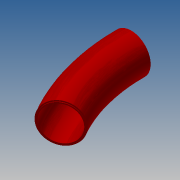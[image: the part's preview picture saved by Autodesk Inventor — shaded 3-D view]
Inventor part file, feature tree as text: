
AUTODESK INVENTOR PART (.ipt)
format: ipt  version: 2017.3 (Build 213257000, 257)  size: 192,000 bytes
history: native  units: in
note: dims shown in document units (in); Inventor stores cm internally (conversion verified against a paired STEP export)
features: extrude x3, sketch x3, revolve x2, fillet x1, chamfer x1
ambient origin geometry x8: Origin, YZ Plane, XZ Plane, XY Plane, X Axis, Y Axis, Z Axis, Center Point
bodies: Solid1 (feature_tree)
feature tree (10):
  revolve  "Revolution1"  [1 undecoded]
  extrude  "Extrusion9"  TaperAngle=30.0deg  [1 undecoded]
  sketch  "Sketch11"  dims[d34=30.5in d35=0.5in d36=0.0in d37=30.48in d38=33.5in d39=0.25in d40=0.0in d41=0.25in d42=0.0in d43=0.0034in d44=0.0312in d45=0.0312in d46=0.125in d47=45.0deg]
  extrude  "Extrusion10"  Depth=0.5in TaperAngle=0.0deg
  extrude  "Extrusion11"  Depth=0.0312in
  revolve  "Revolution2"  [1 undecoded]
  fillet  "Fillet3"  Radius=0.25in
  chamfer  "Chamfer3"  Distance=0.25in
  sketch  "Sketch1"  dims[d0=28.5in d1=32.5in]
  sketch  "Sketch10"  dims[d2=160.0in d3=30.0deg]
note: 3 required parameter values undecoded (feature->parameter linkage not recoverable at this tier; creation-order binding heuristic only, values carry confidence <= 0.55)